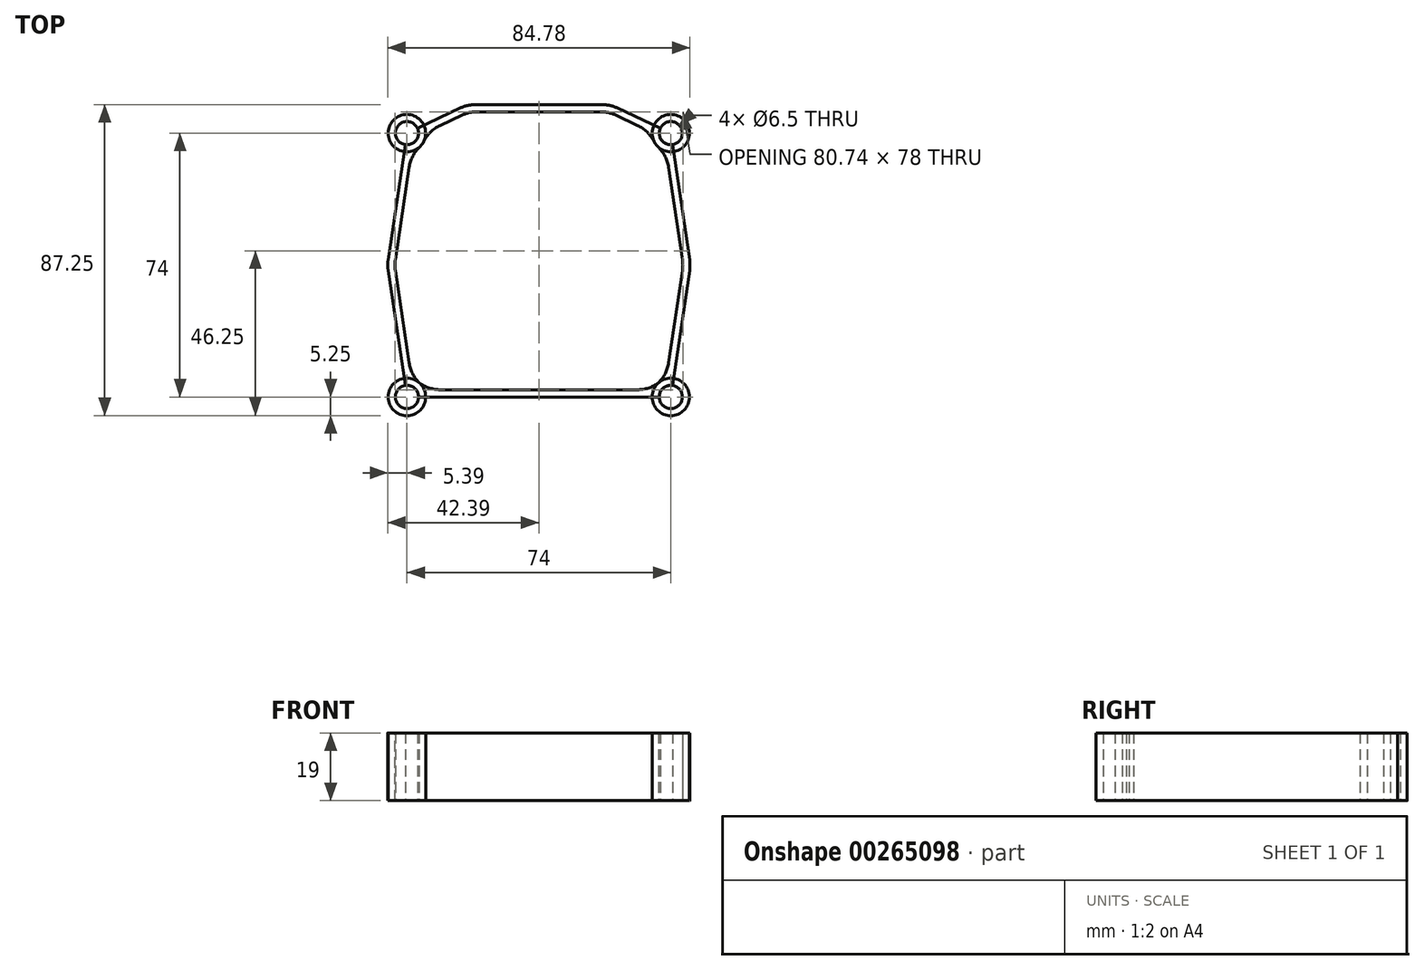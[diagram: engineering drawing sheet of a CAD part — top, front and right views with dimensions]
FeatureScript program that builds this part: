
annotation { "Feature Type Name" : "Feature", "Feature Type Description" : "" }
export const myFeature = defineFeature(function(context is Context, id is Id, definition is map)
    precondition{}
    {
        {
            var Q0;
            Q0=qCreatedBy(makeId("Top.planeOp"),FACE);
            var sketch = newSketch(context, id + "F0", { "sketchPlane" : qUnion([Q0])});
            skCircle(sketch, "E0", {"center": v(-37, 37) * mm, "radius": 5.25 * mm});
            skCircle(sketch, "E1", {"center": v(37, 37) * mm, "radius": 5.25 * mm});
            skCircle(sketch, "E2", {"center": v(37, -37) * mm, "radius": 5.25 * mm});
            skCircle(sketch, "E3", {"center": v(-37, -37) * mm, "radius": 5.25 * mm});
            skLineSegment(sketch, "E4", {"start": v(0, 48.25) * mm, "end": v(0, -59.07) * mm, "construction": true});
            skLineSegment(sketch, "E5", {"start": v(-51.06, 0) * mm, "end": v(61.02, 0) * mm, "construction": true});
            skSolve(sketch);
        }
        {
            var Q0;
            Q0 = qSketchRegion(id + "F0", true);
            extrude(context, id + "F1", {"entities" : qUnion([Q0]), "depth" : 19 * mm});
        }
        {
            var Q0;
            Q0=qCreatedBy(makeId("Top.planeOp"),FACE);
            var sketch = newSketch(context, id + "F2", { "sketchPlane" : qUnion([Q0])});
            skLineSegment(sketch, "E6", {"start": v(-20, 45) * mm, "end": v(20, 45) * mm});
            skLineSegment(sketch, "E7", {"start": v(-37, -37) * mm, "end": v(37, -37) * mm});
            skPoint(sketch, "E8", {"position": v(0, 45) * mm});
            skPoint(sketch, "E9", {"position": v(0, -37) * mm});
            skLineSegment(sketch, "E10", {"start": v(37, -37) * mm, "end": v(42.5, 0) * mm});
            skLineSegment(sketch, "E11", {"start": v(-37, -37) * mm, "end": v(-42.5, 0) * mm});
            skLineSegment(sketch, "E12", {"start": v(-42.5, 0) * mm, "end": v(-37, 37) * mm});
            skLineSegment(sketch, "E13", {"start": v(-37, 37) * mm, "end": v(-20, 45) * mm});
            skLineSegment(sketch, "E14", {"start": v(20, 45) * mm, "end": v(37, 37) * mm});
            skLineSegment(sketch, "E15", {"start": v(37, 37) * mm, "end": v(42.5, 0) * mm});
            skSolve(sketch);
        }
        {
            var Q0;
            Q0 = qSketchRegion(id + "F2", true);
            extrude(context, id + "F3", {"entities" : qUnion([Q0]), "depth" : 19 * mm});
        }
        {
            var Q0;
            Q0=qCreatedBy(makeId("Top.planeOp"),FACE);
            var sketch = newSketch(context, id + "F4", { "sketchPlane" : qUnion([Q0])});
            skCircle(sketch, "E16", {"center": v(-37, 37) * mm, "radius": 3.25 * mm});
            skCircle(sketch, "E17", {"center": v(37, 37) * mm, "radius": 3.25 * mm});
            skCircle(sketch, "E18", {"center": v(37, -37) * mm, "radius": 3.25 * mm});
            skCircle(sketch, "E19", {"center": v(-37, -37) * mm, "radius": 3.25 * mm});
            skSolve(sketch);
        }
        {
            var Q0;
            Q0 = qSketchRegion(id + "F4", true);
            extrude(context, id + "F5", {"entities" : qUnion([Q0]), "operationType" : NewBodyOperationType.REMOVE, "depth" : 25 * mm});
        }
        {
            var Q0;
            Q0=qCreatedBy(makeId("Top.planeOp"),FACE);
            var sketch = newSketch(context, id + "F6", { "sketchPlane" : qUnion([Q0])});
            skLineSegment(sketch, "E20", {"start": v(-19.55, 43) * mm, "end": v(19.55, 43) * mm});
            skArc(sketch, "E21", {"start": v(-35.74, 31.9) * mm, "mid": v(-32.79, 33.87) * mm, "end": v(-31.76, 37.26) * mm});
            skArc(sketch, "E22", {"start": v(31.76, 37.26) * mm, "mid": v(32.79, 33.87) * mm, "end": v(35.74, 31.9) * mm});
            skArc(sketch, "E23", {"start": v(-32.15, -35) * mm, "mid": v(-33.57, -33.02) * mm, "end": v(-35.74, -31.9) * mm});
            skArc(sketch, "E24", {"start": v(35.74, -31.9) * mm, "mid": v(33.57, -33.02) * mm, "end": v(32.15, -35) * mm});
            skLineSegment(sketch, "E25", {"start": v(-19.55, 43) * mm, "end": v(-31.76, 37.26) * mm});
            skLineSegment(sketch, "E26", {"start": v(19.55, 43) * mm, "end": v(31.76, 37.26) * mm});
            skLineSegment(sketch, "E27", {"start": v(-35.74, 31.9) * mm, "end": v(-40.48, 0) * mm});
            skLineSegment(sketch, "E28", {"start": v(-40.48, 0) * mm, "end": v(-35.74, -31.9) * mm});
            skLineSegment(sketch, "E29", {"start": v(-32.15, -35) * mm, "end": v(32.15, -35) * mm});
            skLineSegment(sketch, "E30", {"start": v(35.74, -31.9) * mm, "end": v(40.48, 0) * mm});
            skLineSegment(sketch, "E31", {"start": v(40.48, 0) * mm, "end": v(35.74, 31.9) * mm});
            skSolve(sketch);
        }
        {
            var Q0;
            Q0 = qSketchRegion(id + "F6", true);
            extrude(context, id + "F7", {"entities" : qUnion([Q0]), "operationType" : NewBodyOperationType.REMOVE, "depth" : 25 * mm});
        }
        {
            var Q0;
            Q0=makeQuery(id+"F3.opExtrude","SWEPT_EDGE",EDGE,{"disambiguationData":[OSD([sQuery(id+"F2.wireOp",EDGE,"E10"),sQuery(id+"F2.wireOp",EDGE,"E15")])]});
            var Q1;
            Q1=makeQuery(id+"F3.opExtrude","SWEPT_EDGE",EDGE,{"disambiguationData":[OSD([sQuery(id+"F2.wireOp",EDGE,"E11"),sQuery(id+"F2.wireOp",EDGE,"E12")])]});
            var Q2;
            Q2=makeQuery(id+"F3.opExtrude","SWEPT_EDGE",EDGE,{"disambiguationData":[OSD([sQuery(id+"F2.wireOp",EDGE,"E6"),sQuery(id+"F2.wireOp",EDGE,"E13")])]});
            var Q3;
            Q3=makeQuery(id+"F3.opExtrude","SWEPT_EDGE",EDGE,{"disambiguationData":[OSD([sQuery(id+"F2.wireOp",EDGE,"E6"),sQuery(id+"F2.wireOp",EDGE,"E14")])]});
            var Q4;
            Q4=makeQuery(id+"F7.boolean.opBoolean","COPY",EDGE,{"derivedFrom":makeQuery(id+"F7.opExtrude","SWEPT_EDGE",EDGE,{"disambiguationData":[OSD([sQuery(id+"F6.wireOp",EDGE,"E20"),sQuery(id+"F6.wireOp",EDGE,"E26")])]})});
            var Q5;
            Q5=makeQuery(id+"F7.boolean.opBoolean","COPY",EDGE,{"derivedFrom":makeQuery(id+"F7.opExtrude","SWEPT_EDGE",EDGE,{"disambiguationData":[OSD([sQuery(id+"F6.wireOp",EDGE,"E20"),sQuery(id+"F6.wireOp",EDGE,"E25")])]})});
            var Q6;
            Q6=makeQuery(id+"F7.boolean.opBoolean","COPY",EDGE,{"derivedFrom":makeQuery(id+"F7.opExtrude","SWEPT_EDGE",EDGE,{"disambiguationData":[OSD([sQuery(id+"F6.wireOp",EDGE,"E27"),sQuery(id+"F6.wireOp",EDGE,"E28")])]})});
            var Q7;
            Q7=makeQuery(id+"F7.boolean.opBoolean","COPY",EDGE,{"derivedFrom":makeQuery(id+"F7.opExtrude","SWEPT_EDGE",EDGE,{"disambiguationData":[OSD([sQuery(id+"F6.wireOp",EDGE,"E30"),sQuery(id+"F6.wireOp",EDGE,"E31")])]})});
            var Q8;
            Q8=makeQuery(id+"F7.boolean.opBoolean","COPY",EDGE,{"derivedFrom":makeQuery(id+"F7.opExtrude","SWEPT_EDGE",EDGE,{"disambiguationData":[OSD([sQuery(id+"F6.wireOp",EDGE,"E21"),sQuery(id+"F6.wireOp",EDGE,"E27")])]})});
            var Q9;
            Q9=makeQuery(id+"F7.boolean.opBoolean","COPY",EDGE,{"derivedFrom":makeQuery(id+"F7.opExtrude","SWEPT_EDGE",EDGE,{"disambiguationData":[OSD([sQuery(id+"F6.wireOp",EDGE,"E21"),sQuery(id+"F6.wireOp",EDGE,"E25")])]})});
            var Q10;
            Q10=makeQuery(id+"F7.boolean.opBoolean","COPY",EDGE,{"derivedFrom":makeQuery(id+"F7.opExtrude","SWEPT_EDGE",EDGE,{"disambiguationData":[OSD([sQuery(id+"F6.wireOp",EDGE,"E23"),sQuery(id+"F6.wireOp",EDGE,"E28")])]})});
            var Q11;
            Q11=makeQuery(id+"F7.boolean.opBoolean","COPY",EDGE,{"derivedFrom":makeQuery(id+"F7.opExtrude","SWEPT_EDGE",EDGE,{"disambiguationData":[OSD([sQuery(id+"F6.wireOp",EDGE,"E23"),sQuery(id+"F6.wireOp",EDGE,"E29")])]})});
            var Q12;
            Q12=makeQuery(id+"F7.boolean.opBoolean","COPY",EDGE,{"derivedFrom":makeQuery(id+"F7.opExtrude","SWEPT_EDGE",EDGE,{"disambiguationData":[OSD([sQuery(id+"F6.wireOp",EDGE,"E22"),sQuery(id+"F6.wireOp",EDGE,"E31")])]})});
            var Q13;
            Q13=makeQuery(id+"F7.boolean.opBoolean","COPY",EDGE,{"derivedFrom":makeQuery(id+"F7.opExtrude","SWEPT_EDGE",EDGE,{"disambiguationData":[OSD([sQuery(id+"F6.wireOp",EDGE,"E22"),sQuery(id+"F6.wireOp",EDGE,"E26")])]})});
            var Q14;
            Q14=makeQuery(id+"F7.boolean.opBoolean","COPY",EDGE,{"derivedFrom":makeQuery(id+"F7.opExtrude","SWEPT_EDGE",EDGE,{"disambiguationData":[OSD([sQuery(id+"F6.wireOp",EDGE,"E24"),sQuery(id+"F6.wireOp",EDGE,"E29")])]})});
            var Q15;
            Q15=makeQuery(id+"F7.boolean.opBoolean","COPY",EDGE,{"derivedFrom":makeQuery(id+"F7.opExtrude","SWEPT_EDGE",EDGE,{"disambiguationData":[OSD([sQuery(id+"F6.wireOp",EDGE,"E24"),sQuery(id+"F6.wireOp",EDGE,"E30")])]})});
            fillet(context, id + "F8", {"entities" : qUnion([Q0, Q1, Q2, Q3, Q4, Q5, Q6, Q7, Q8, Q9, Q10, Q11, Q12, Q13, Q14, Q15]), "radius" : 10 * mm, "tangentPropagation" : true, "allowEdgeOverflow" : false});
        }
    });
